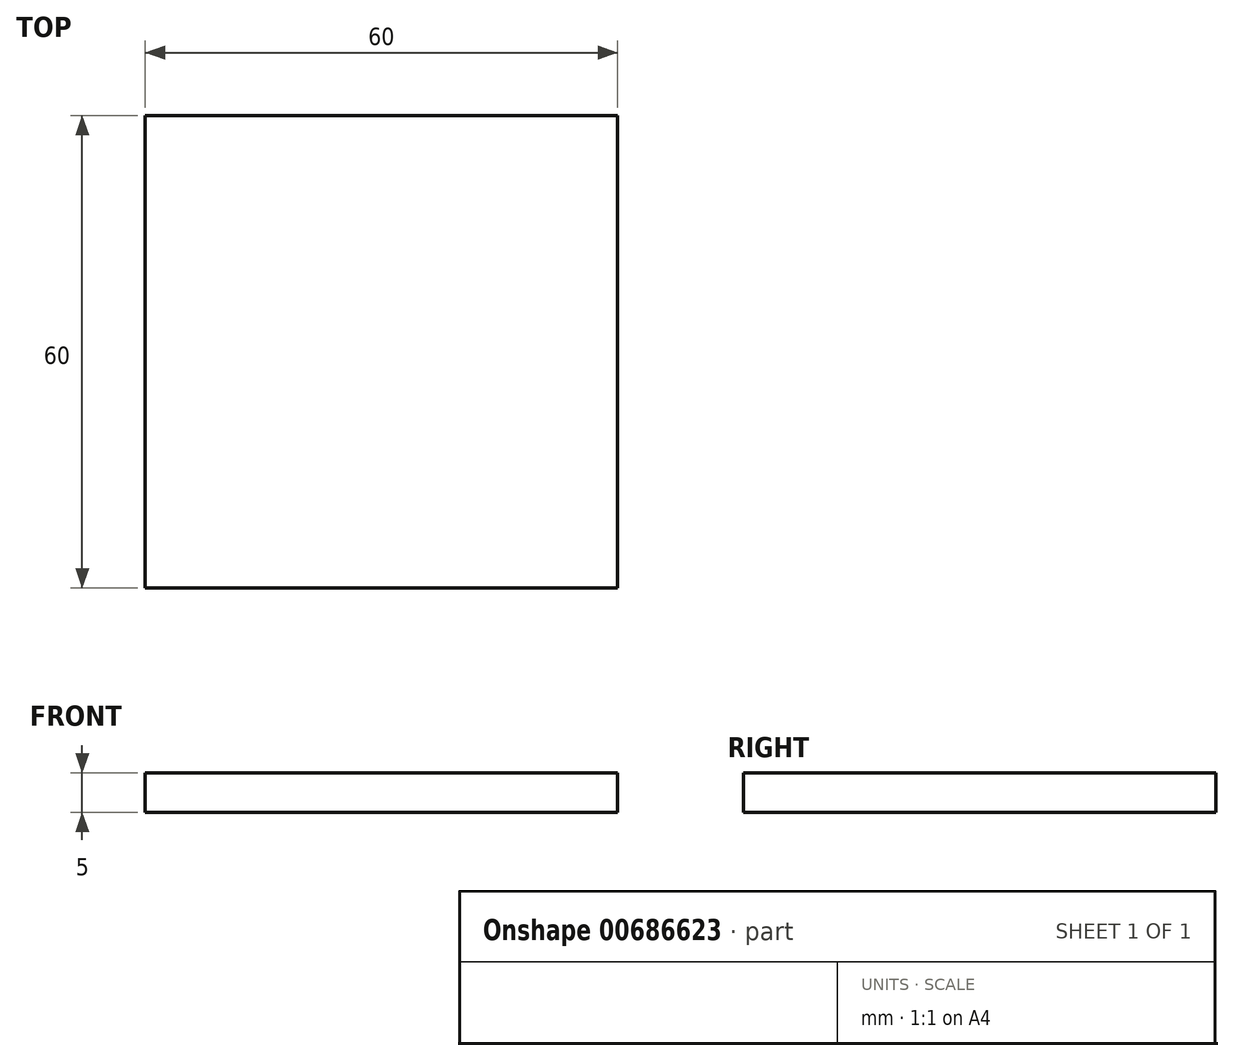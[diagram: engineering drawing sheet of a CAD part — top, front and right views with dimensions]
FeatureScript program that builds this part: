
annotation { "Feature Type Name" : "Feature", "Feature Type Description" : "" }
export const myFeature = defineFeature(function(context is Context, id is Id, definition is map)
    precondition{}
    {
        {
            var Q0;
            Q0=qCreatedBy(makeId("Top.planeOp"),FACE);
            var sketch = newSketch(context, id + "F0", { "sketchPlane" : qUnion([Q0])});
            skLineSegment(sketch, "E0.bottom", {"start": v(-15.16, 16.87) * mm, "end": v(44.84, 16.87) * mm});
            skLineSegment(sketch, "E0.top", {"start": v(-15.16, -43.13) * mm, "end": v(44.84, -43.13) * mm});
            skLineSegment(sketch, "E0.left", {"start": v(-15.16, 16.87) * mm, "end": v(-15.16, -43.13) * mm});
            skLineSegment(sketch, "E0.right", {"start": v(44.84, 16.87) * mm, "end": v(44.84, -43.13) * mm});
            skSolve(sketch);
        }
        {
            var Q0;
            Q0=makeQuery(id+"F0.imprint","IMPRINT",FACE,{"disambiguationData":[TD([[makeQuery(id+"F0.imprint","IMPRINT",EDGE,{"derivedFrom":sQuery(id+"F0.wireOp",EDGE,"E0.bottom")}),-1.0]])]});
            extrude(context, id + "F1", {"entities" : qUnion([Q0]), "depth" : 5 * mm, "offsetDistance" : 25.4 * mm});
        }
    });
